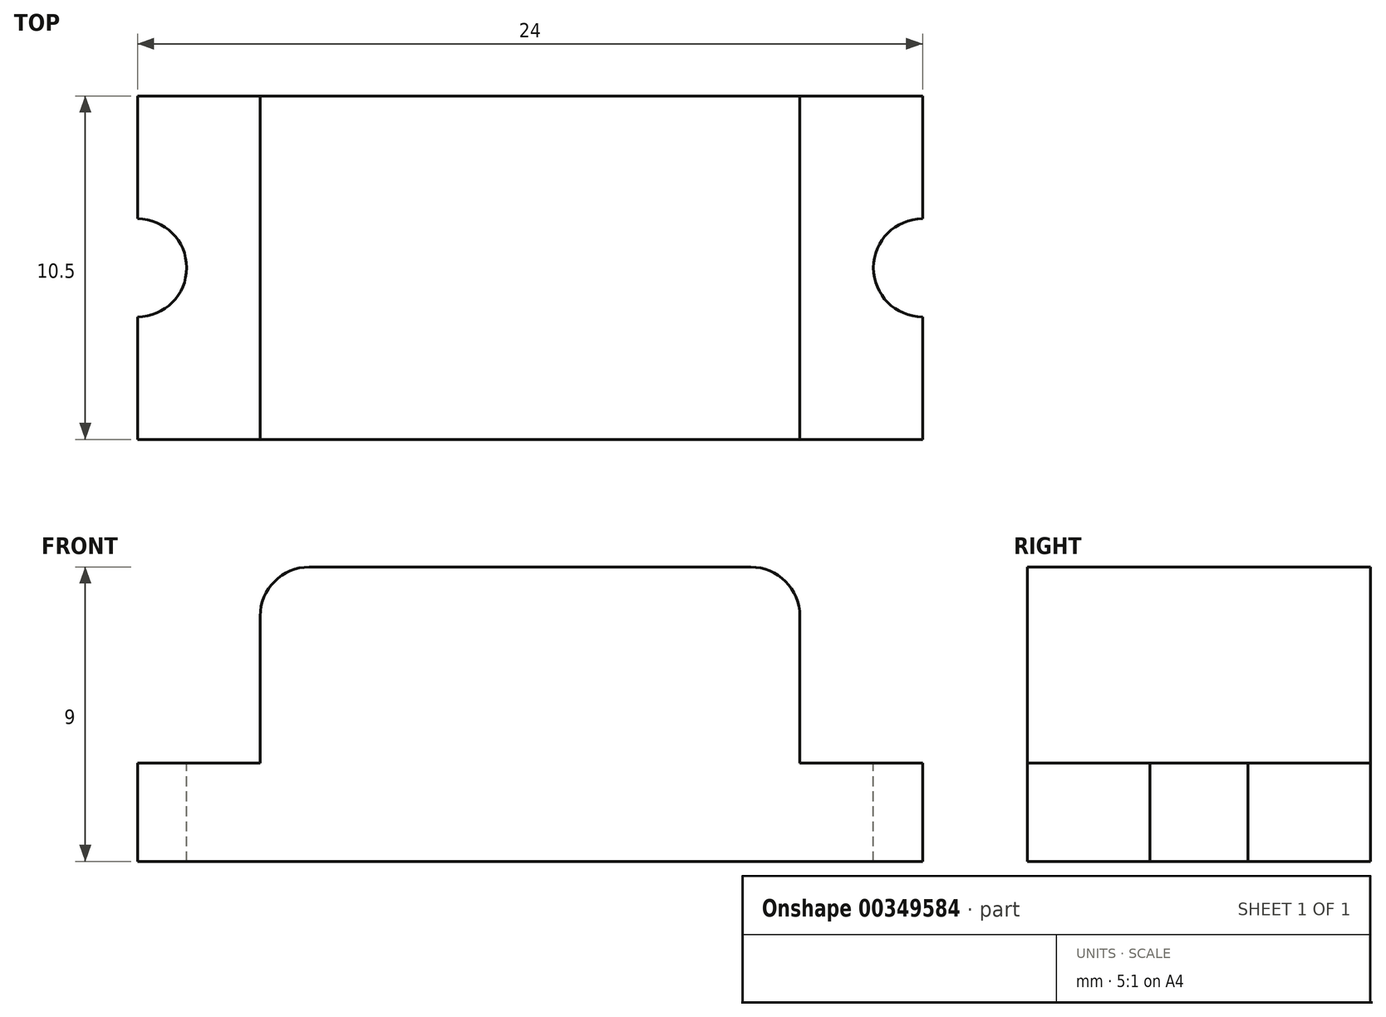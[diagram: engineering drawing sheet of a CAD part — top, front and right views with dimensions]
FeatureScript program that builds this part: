
annotation { "Feature Type Name" : "Feature", "Feature Type Description" : "" }
export const myFeature = defineFeature(function(context is Context, id is Id, definition is map)
    precondition{}
    {
        {
            var Q0;
            Q0=qCreatedBy(makeId("Front.planeOp"),FACE);
            var sketch = newSketch(context, id + "F0", { "sketchPlane" : qUnion([Q0])});
            skLineSegment(sketch, "E0.bottom", {"start": v(-0.55, 0) * mm, "end": v(0.55, 0) * mm});
            skLineSegment(sketch, "E0.top", {"start": v(-0.55, 0.4) * mm, "end": v(0.55, 0.4) * mm});
            skLineSegment(sketch, "E0.left", {"start": v(-0.55, 0) * mm, "end": v(-0.55, 0.4) * mm});
            skLineSegment(sketch, "E0.right", {"start": v(0.55, 0) * mm, "end": v(0.55, 0.4) * mm});
            skLineSegment(sketch, "E1.bottom", {"start": v(-0.8, 0) * mm, "end": v(0.8, 0) * mm});
            skLineSegment(sketch, "E1.top", {"start": v(-0.8, -0.2) * mm, "end": v(0.8, -0.2) * mm});
            skLineSegment(sketch, "E1.left", {"start": v(-0.8, 0) * mm, "end": v(-0.8, -0.2) * mm});
            skLineSegment(sketch, "E1.right", {"start": v(0.8, 0) * mm, "end": v(0.8, -0.2) * mm});
            skSolve(sketch);
        }
        {
            var Q0;
            Q0=qSketchRegion(id+"F0",true);
            extrude(context, id + "F1", {"entities" : qUnion([Q0]), "depth" : .7 * mm});
        }
        {
            var Q0;
            Q0=makeQuery(id+"F1.opExtrude","SWEPT_EDGE",EDGE,{"disambiguationData":[OSD([sQuery(id+"F0.wireOp",EDGE,"E0.top"),sQuery(id+"F0.wireOp",EDGE,"E0.left")])]});
            var Q1;
            Q1=makeQuery(id+"F1.opExtrude","SWEPT_EDGE",EDGE,{"disambiguationData":[OSD([sQuery(id+"F0.wireOp",EDGE,"E0.top"),sQuery(id+"F0.wireOp",EDGE,"E0.right")])]});
            fillet(context, id + "F2", {"entities" : qUnion([Q0, Q1]), "radius" : .1 * mm, "tangentPropagation" : true, "allowEdgeOverflow" : false});
        }
        {
            var Q0;
            {var subQ0=sQuery(id+"F0.wireOp",EDGE,"E1.bottom");Q0=makeQuery(id+"F1.opExtrude","SWEPT_FACE",FACE,{"disambiguationData":[OSD([subQ0]),TDD([makeQuery(id+"F0.imprint","IMPRINT",EDGE,{"disambiguationData":[TD([[makeQuery(id+"F0.imprint","INTERSECT",VERTEX,{"derivedFrom":[sQuery(id+"F0.wireOp",EDGE,"E0.left"),subQ0]}),1.0]])],"derivedFrom":subQ0})])]});}
            var sketch = newSketch(context, id + "F3", { "sketchPlane" : qUnion([Q0])});
            skArc(sketch, "E2", {"start": v(-0.8, -0.45) * mm, "mid": v(-0.7, -0.35) * mm, "end": v(-0.8, -0.25) * mm});
            skArc(sketch, "E3", {"start": v(0.8, -0.25) * mm, "mid": v(0.7, -0.35) * mm, "end": v(0.8, -0.45) * mm});
            skLineSegment(sketch, "E4", {"start": v(-0.8, -0.25) * mm, "end": v(-0.8, -0.45) * mm});
            skLineSegment(sketch, "E5", {"start": v(0.8, -0.25) * mm, "end": v(0.8, -0.45) * mm});
            skSolve(sketch);
        }
        {
            var Q0;
            Q0=qSketchRegion(id+"F3",true);
            extrude(context, id + "F4", {"entities" : qUnion([Q0]), "operationType" : NewBodyOperationType.REMOVE, "oppositeDirection" : true, "depth" : 25 * mm});
        }
        {
            var Q0;
            Q0=makeQuery(id+"F1.opExtrude","SWEPT_BODY",BODY,{"disambiguationData":[OSD([sQuery(id+"F0.wireOp",EDGE,"E0.top"),sQuery(id+"F0.wireOp",EDGE,"E0.left"),sQuery(id+"F0.wireOp",EDGE,"E0.right"),sQuery(id+"F0.wireOp",EDGE,"E1.bottom"),sQuery(id+"F0.wireOp",EDGE,"E1.top"),sQuery(id+"F0.wireOp",EDGE,"E1.left"),sQuery(id+"F0.wireOp",EDGE,"E1.right")])]});
            var Q1;
            Q1=qCreatedBy(makeId("Origin.pointOp"),VERTEX);
            transform(context, id + "F5", {"entities" : qUnion([Q0]), "transformType" : TransformType.SCALE_UNIFORMLY, "scale" : 15, "scalePoint" : qUnion([Q1]), "makeCopy" : false});
        }
    });
